# Revit family: 0039348+0039356 Feilo Sylvania Lighting Fixture START HIGHBAY 4K 19KLM WIDE with ALU SHADE ALU COLOR FOR 13_19KLM
name_source: partatom
category: Lighting Fixtures
revit_build: Autodesk Revit 2017 (Build: 20190507_1515(x64)
units: mm (PartAtom-declared; Revit-internal decimal feet)

## family parameters
Cut with Voids When Loaded = No
Host = Face
Light Source = Yes
OmniClass Number = 23.80.70.00
OmniClass Title = Lighting
Part Type = Normal
Room Calculation Point = No
Round Connector Dimension = Use Diameter
Shared = No

## types (1)
- 0039348+0039356 START HIGHBAY 4K 19KLM WIDE ALU SHADE ALU COLOR FOR 13/19KLM
    Apparent Load = 150 VA
    Assembly Code = D5020200
    AssetType = Fixed
    ClassificationName = Uniclass2015
    ClassificationValue = EF_70_80
    Color Filter = 16777215
    Cost = 0 $
    Default Elevation = 1219 mm
    Description = START HIGHBAY, includes 1 m cables, black aluminium housing, 19500LM, 150W, 130lm/W, 4000K, Driver current: 3210mA, CR80, 90° beam angle, 1-10V dimmable,  IP65, IK08, 50,000 hrs (L70B50), (LxWxH) 296x296x177mm
    DiameterWireSupport_FEILO = 10 mm  [stored 0.0328084 ft]
    DiameterWire_FEILO = 3 mm  [stored 0.00984252 ft]
    Dimming Lamp Color Temperature Shift = <None>
    DocumentationLiterature = http://www.sylvania-lighting.com
    DriverBottom_FEILO = 65 mm
    DriverRadiusTop_FEILO = 45 mm
    DriverRadius_FEILO = 67 mm
    DriverVerticalChamfer_FEILO = 8 mm  [stored 0.0262467 ft]
    DriverVerticalStraight_FEILO = 50 mm  [stored 0.164042 ft]
    DurationUnit = hours
    ElectricShockClassification = Class I
    Emit Shape Visible in Rendering = No
    Emit from Circle Diameter = 211 mm
    ExpectedLife = 50000
    EyeInner_FEILO = 15 mm
    EyeThicknessHalf_FEILO = 5 mm  [stored 0.0164042 ft]
    EyeThickness_FEILO = 9 mm  [stored 0.0295276 ft]
    HeightRingChamfer_FEILO = 23 mm
    HeightRing_FEILO = 32 mm  [stored 0.104987 ft]
    IfcExportAs = IfcLightFixtureType
    IfcExportType = IfcLightFixtureType
    ImpactProtectionIndex = IK08
    IngressProtection = IP65
    InputNominalFrequency = 50/60 Hz
    InputVoltage = 220-240V~
    Keynote = 16500
    Lamp = LED
    LampColourRenderingIndex = 80
    LampColourTemperature = 4000 K
    LampNominalLuminous = 19500 lm
    LampsType = LED
    LuminousEfficacy = 130 lm/W
    Manufacturer = Feilo Sylvania
    ManufacturerName = Feilo Sylvania
    Material = aluminium alloy housing, polycarbonate diffuser
    Material_1_FEILO = Body-Sylvania-StartHighbay-Black
    Material_2_FEILO = Diffuser-Sylvania-StartHighbay-Transparent
    Material_3_FEILO = LED-Sylvania-StartHighbay-Glow
    Material_4_FEILO = Shade-Sylvania-StartHighbay-Alu
    Material_5_FEILO = Shade-Sylvania-StartHighbay-Alu
    Model = START HIGHBAY 4K 19KLM WIDE ALU SHADE ALU COLOR FOR 13/19KLM
    ModelNumber = 0039348+0039356
    ModelReference = START HIGHBAY 4K 19KLM WIDE ALU SHADE ALU COLOR FOR 13/19KLM
    Name = START HIGHBAY 4K 19KLM WIDE ALU SHADE ALU COLOR FOR 13/19KLM
    NominalDepth = 296 mm
    NominalHeight = 177 mm
    NominalLength = 296 mm
    Photometric Web File = 0039348+0039356.ies
    PowerConsumption = 150 W
    PowerFactor = 0.95
    RHHeight1_FEILO = 15 mm
    RHHeight2_FEILO = 2 mm  [stored 0.00656168 ft]
    RHHeight3_FEILO = 4 mm  [stored 0.0131234 ft]
    RHHeight4_FEILO = 8 mm  [stored 0.0262467 ft]
    RHRadius1_FEILO = 15 mm
    RHRadius2_FEILO = 12 mm  [stored 0.0393701 ft]
    RHRadius3_FEILO = 7 mm  [stored 0.0229659 ft]
    RadiusArrayPost_FEILO = 61 mm
    RadiusDiffuser_FEILO = 105 mm
    Radius_FEILO = 148 mm  [stored 0.485564 ft]
    Rib1_FEILO = 17 mm
    Rib2_FEILO = 4 mm  [stored 0.0131234 ft]
    Rib3_FEILO = 18 mm
    Rib4_FEILO = 14 mm  [stored 0.0459318 ft]
    ShadeHeight_FEILO = 120 mm  [stored 0.393701 ft]
    ShadeRadiusBend_FEILO = 210 mm  [stored 0.688976 ft]
    ShadeRadiusIn_FEILO = 95 mm  [stored 0.31168 ft]
    ShadeRadiusOut_FEILO = 205 mm
    ShadeSizeSM_FEILO = Yes
    ShadeThickness_FEILO = 3 mm  [stored 0.00984252 ft]
    SizeM_FEILO = Yes
    SizeS_FEILO = No
    ThicknessBracketHalf_FEILO = 1 mm  [stored 0.00328084 ft]
    ThicknessBracket_FEILO = 2 mm  [stored 0.00656168 ft]
    ThicknessWall_FEILO = 2 mm  [stored 0.00656168 ft]
    Tilt Angle = -90.00°
    Type Image = <None>
    TypeName = START HIGHBAY 4K 19KLM WIDE ALU SHADE ALU COLOR FOR 13/19KLM
    URL = http://www.sylvania-lighting.com
    VisibilityBracket_FEILO = No
    Voltage = 230 V
    Weight = 3.4 kg
    WidthBracket_FEILO = 40 mm  [stored 0.131234 ft]
    WidthCurvedRing_FEILO = 4 mm  [stored 0.0131234 ft]
    WidthCurved_FEILO = 16 mm
    WidthRingChamfer_FEILO = 11 mm  [stored 0.0360892 ft]
    WidthStraight_FEILO = 4 mm  [stored 0.0131234 ft]

note: [stored X ft] marks values corroborated as IEEE doubles in the binary element streams (Revit-internal decimal feet)

## geometry (parser evidence)
native form markers: Sweep x2
no freeform markers — native parametric forms only
